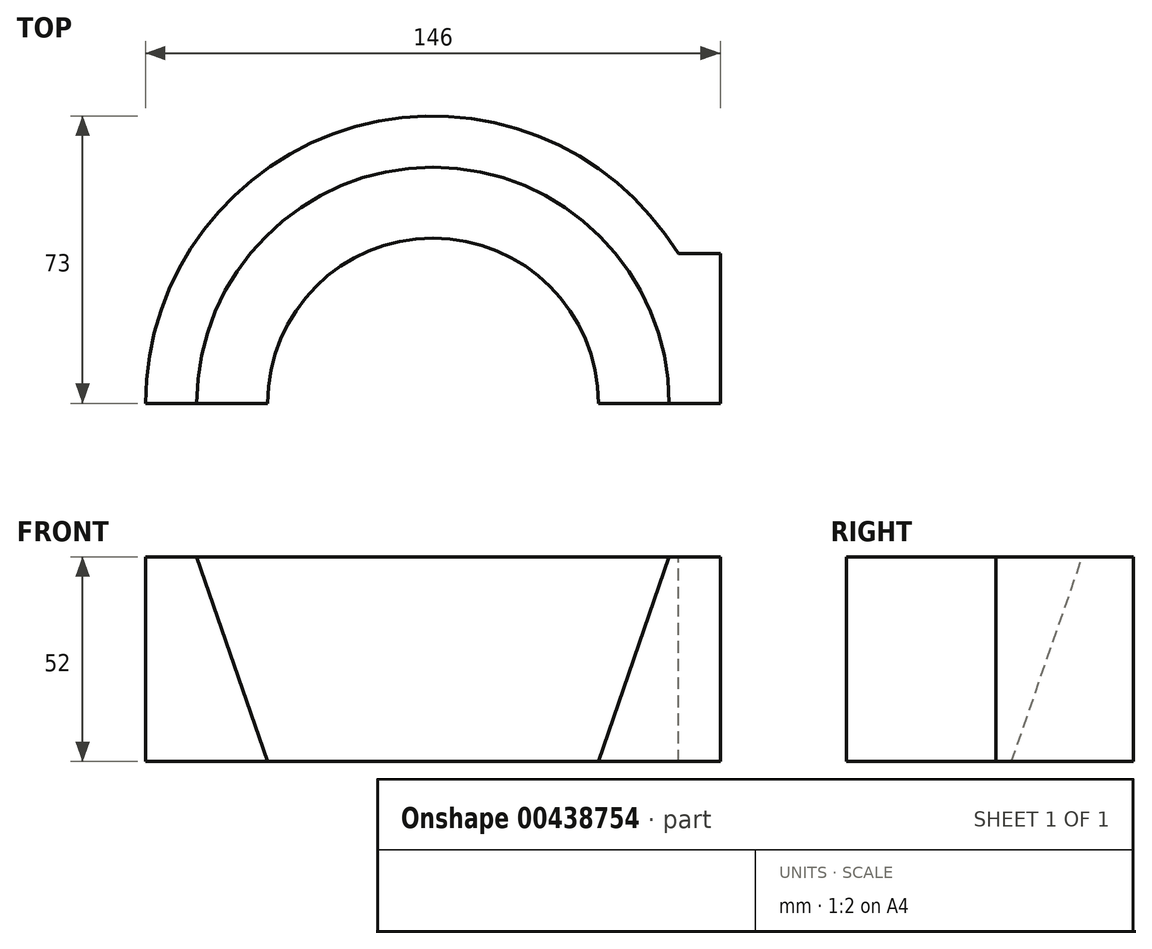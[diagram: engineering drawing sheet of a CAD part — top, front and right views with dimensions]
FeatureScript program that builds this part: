
annotation { "Feature Type Name" : "Feature", "Feature Type Description" : "" }
export const myFeature = defineFeature(function(context is Context, id is Id, definition is map)
    precondition{}
    {
        {
            var Q0;
            Q0=qCreatedBy(makeId("Front.planeOp"),FACE);
            var sketch = newSketch(context, id + "F0", { "sketchPlane" : qUnion([Q0])});
            skLineSegment(sketch, "E0", {"start": v(-73, 0) * mm, "end": v(-42, 0) * mm});
            skLineSegment(sketch, "E1", {"start": v(-42, 0) * mm, "end": v(-60, 52) * mm});
            skLineSegment(sketch, "E2", {"start": v(-60, 52) * mm, "end": v(-73, 52) * mm});
            skLineSegment(sketch, "E3", {"start": v(-73, 52) * mm, "end": v(-73, 0) * mm});
            skLineSegment(sketch, "E4", {"start": v(0, 73.5) * mm, "end": v(0, -56.14) * mm});
            skSolve(sketch);
        }
        {
            var Q0;
            Q0 = qSketchRegion(id + "F0", true);
            var Q1;
            Q1=sQuery(id+"F0.wireOp",EDGE,"E4");
            revolve(context, id + "F1", {"entities" : qUnion([Q0]), "axis" : qUnion([Q1]), "revolveType" : RevolveType.ONE_DIRECTION, "angle" : 180 * degree});
        }
        {
            var Q0;
            Q0=makeQuery(id+"F1.opRevolve","CAP_FACE",FACE,{"disambiguationData":[OSD([sQuery(id+"F0.wireOp",EDGE,"E0"),sQuery(id+"F0.wireOp",EDGE,"E1"),sQuery(id+"F0.wireOp",EDGE,"E2"),sQuery(id+"F0.wireOp",EDGE,"E3")])],"isStart":false});
            var sketch = newSketch(context, id + "F2", { "sketchPlane" : qUnion([Q0])});
            skLineSegment(sketch, "E5", {"start": v(42, 0) * mm, "end": v(156, 0) * mm});
            skLineSegment(sketch, "E6", {"start": v(156, 0) * mm, "end": v(156, 52) * mm, "construction": true});
            skLineSegment(sketch, "E7", {"start": v(156, 52) * mm, "end": v(60, 52) * mm});
            skLineSegment(sketch, "E8.0", {"start": v(42, 0) * mm, "end": v(60, 52) * mm});
            skArc(sketch, "E9", {"start": v(156, 52) * mm, "mid": v(182, 26) * mm, "end": v(156, 0) * mm});
            skCircle(sketch, "E10", {"center": v(156, 26) * mm, "radius": 11 * mm});
            skCircle(sketch, "E11", {"center": v(108, 26) * mm, "radius": 11 * mm});
            skSolve(sketch);
        }
        {
            var Q0;
            {var subQ0=sQuery(id+"F2.wireOp",EDGE,"E9");Q0=makeQuery(id+"F2.imprint","IMPRINT",FACE,{"disambiguationData":[TD([[makeQuery(id+"F2.imprint","IMPRINT",EDGE,{"derivedFrom":subQ0}),-1.0]])]});}
            var Q1;
            {var subQ2=sQuery(id+"F2.wireOp",EDGE,"E8.0");Q1=makeQuery(id+"F2.imprint","IMPRINT",FACE,{"disambiguationData":[TD([[makeQuery(id+"F2.imprint","IMPRINT",EDGE,{"derivedFrom":subQ2}),-1.0]])]});}
            extrude(context, id + "F3", {"entities" : qUnion([Q0, Q1]), "operationType" : NewBodyOperationType.ADD, "oppositeDirection" : true, "depth" : 38 * mm});
        }
    });
